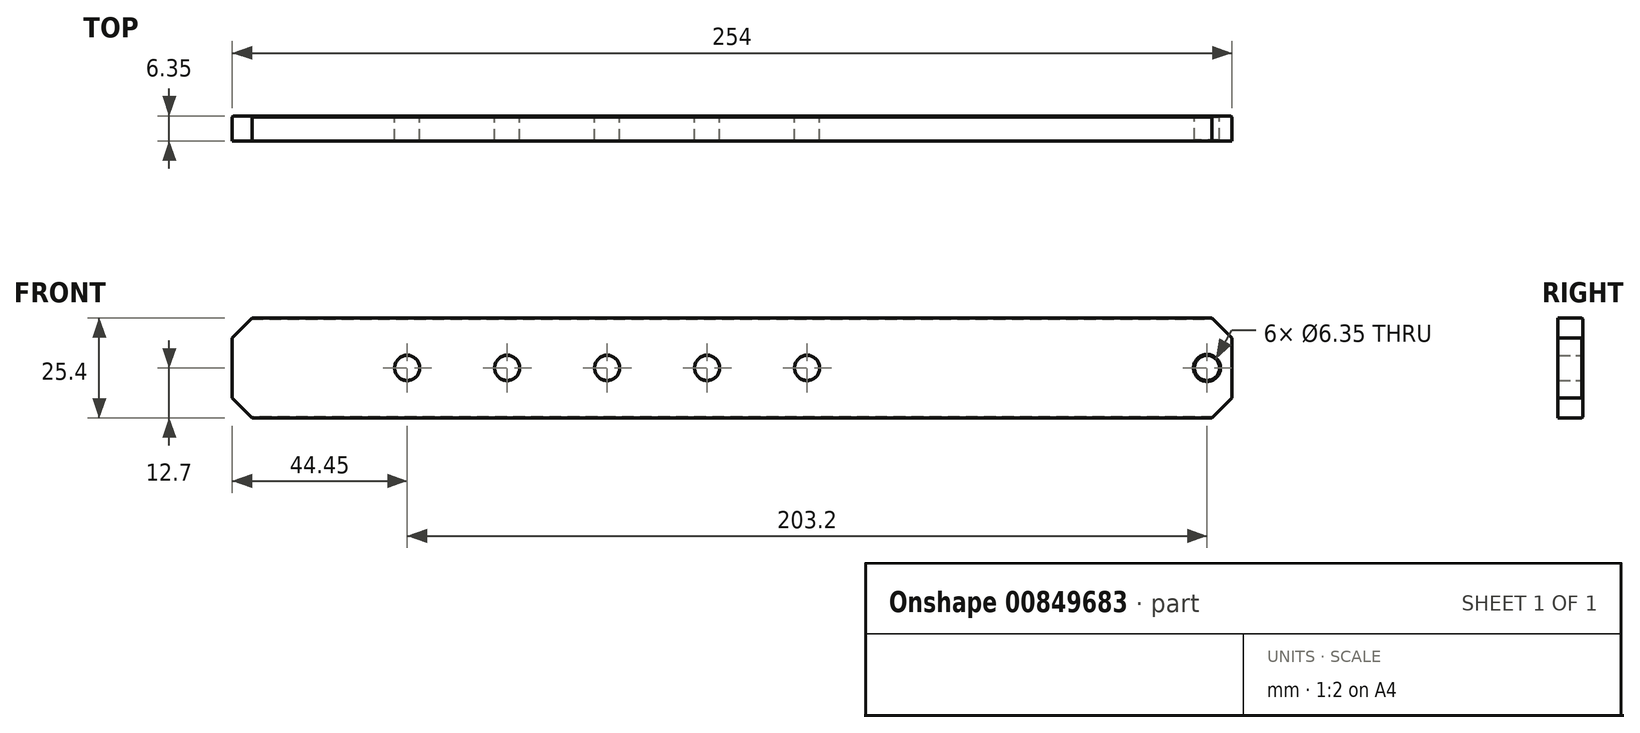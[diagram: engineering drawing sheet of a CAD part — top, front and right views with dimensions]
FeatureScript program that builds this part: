
annotation { "Feature Type Name" : "Feature", "Feature Type Description" : "" }
export const myFeature = defineFeature(function(context is Context, id is Id, definition is map)
    precondition{}
    {
        {
            var Q0;
            Q0=qCreatedBy(makeId("Front.planeOp"),FACE);
            var sketch = newSketch(context, id + "F0", { "sketchPlane" : qUnion([Q0])});
            skLineSegment(sketch, "E0.bottom", {"start": v(127, -12.7) * mm, "end": v(-127, -12.7) * mm});
            skLineSegment(sketch, "E0.top", {"start": v(127, 12.7) * mm, "end": v(-127, 12.7) * mm});
            skLineSegment(sketch, "E0.left", {"start": v(127, -12.7) * mm, "end": v(127, 12.7) * mm});
            skLineSegment(sketch, "E0.right", {"start": v(-127, -12.7) * mm, "end": v(-127, 12.7) * mm});
            skPoint(sketch, "E0.middle", {"position": v(0, 0) * mm});
            skCircle(sketch, "E1", {"center": v(120.65, 0) * mm, "radius": 3.18 * mm});
            skLineSegment(sketch, "E2", {"start": v(120.65, 0) * mm, "end": v(-127, 0) * mm, "construction": true});
            skCircle(sketch, "E3", {"center": v(19.05, 0) * mm, "radius": 3.18 * mm});
            skCircle(sketch, "E4.1.0.0", {"center": v(-6.35, 0) * mm, "radius": 3.18 * mm});
            skCircle(sketch, "E4.2.0.0", {"center": v(-31.75, 0) * mm, "radius": 3.18 * mm});
            skCircle(sketch, "E4.3.0.0", {"center": v(-57.15, 0) * mm, "radius": 3.18 * mm});
            skCircle(sketch, "E4.4.0.0", {"center": v(-82.55, 0) * mm, "radius": 3.18 * mm});
            skLineSegment(sketch, "E4.direction1", {"start": v(19.05, 0) * mm, "end": v(-6.35, 0) * mm, "construction": true});
            skSolve(sketch);
        }
        {
            var Q0;
            Q0 = qSketchRegion(id + "F0", true);
            extrude(context, id + "F1", {"entities" : qUnion([Q0]), "depth" : 6.35 * mm, "offsetDistance" : 25.4 * mm});
        }
        {
            var Q0;
            Q0=makeQuery(id+"F1.opExtrude","CAP_EDGE",EDGE,{"disambiguationData":[OSD([sQuery(id+"F0.wireOp",EDGE,"a60a66de-6e48-4f97-a744-45ec2d759609.0.4.0")])],"isStart":false});
            var Q1;
            Q1=makeQuery(id+"F1.opExtrude","CAP_EDGE",EDGE,{"disambiguationData":[OSD([sQuery(id+"F0.wireOp",EDGE,"d8a7950c-4cc1-41c2-8a6e-5c12bcb3506b.3.0.0")])],"isStart":false});
            var Q2;
            Q2=makeQuery(id+"F1.opExtrude","CAP_EDGE",EDGE,{"disambiguationData":[OSD([sQuery(id+"F0.wireOp",EDGE,"d8a7950c-4cc1-41c2-8a6e-5c12bcb3506b.2.0.0")])],"isStart":false});
            var Q3;
            Q3=makeQuery(id+"F1.opExtrude","CAP_EDGE",EDGE,{"disambiguationData":[OSD([sQuery(id+"F0.wireOp",EDGE,"d8a7950c-4cc1-41c2-8a6e-5c12bcb3506b.1.0.0")])],"isStart":false});
            var Q4;
            Q4=makeQuery(id+"F1.opExtrude","CAP_EDGE",EDGE,{"disambiguationData":[OSD([sQuery(id+"F0.wireOp",EDGE,"ClvN4MZP-DohT-0DrA-vtji-N6Pn7AbvIDh7")])],"isStart":false});
            var Q5;
            Q5=makeQuery(id+"F1.opExtrude","CAP_EDGE",EDGE,{"disambiguationData":[OSD([sQuery(id+"F0.wireOp",EDGE,"E1")])],"isStart":false});
            var Q6;
            Q6=makeQuery(id+"F1.opExtrude","CAP_EDGE",EDGE,{"disambiguationData":[OSD([sQuery(id+"F0.wireOp",EDGE,"E1")])],"isStart":true});
            var Q7;
            Q7=makeQuery(id+"F1.opExtrude","CAP_EDGE",EDGE,{"disambiguationData":[OSD([sQuery(id+"F0.wireOp",EDGE,"ClvN4MZP-DohT-0DrA-vtji-N6Pn7AbvIDh7")])],"isStart":true});
            var Q8;
            Q8=makeQuery(id+"F1.opExtrude","CAP_EDGE",EDGE,{"disambiguationData":[OSD([sQuery(id+"F0.wireOp",EDGE,"d8a7950c-4cc1-41c2-8a6e-5c12bcb3506b.1.0.0")])],"isStart":true});
            var Q9;
            Q9=makeQuery(id+"F1.opExtrude","CAP_FACE",FACE,{"disambiguationData":[OSD([sQuery(id+"F0.wireOp",EDGE,"E0.bottom"),sQuery(id+"F0.wireOp",EDGE,"E0.top"),sQuery(id+"F0.wireOp",EDGE,"E0.left"),sQuery(id+"F0.wireOp",EDGE,"E0.right"),sQuery(id+"F0.wireOp",EDGE,"E1"),sQuery(id+"F0.wireOp",EDGE,"ClvN4MZP-DohT-0DrA-vtji-N6Pn7AbvIDh7"),sQuery(id+"F0.wireOp",EDGE,"d8a7950c-4cc1-41c2-8a6e-5c12bcb3506b.1.0.0"),sQuery(id+"F0.wireOp",EDGE,"d8a7950c-4cc1-41c2-8a6e-5c12bcb3506b.2.0.0"),sQuery(id+"F0.wireOp",EDGE,"d8a7950c-4cc1-41c2-8a6e-5c12bcb3506b.3.0.0"),sQuery(id+"F0.wireOp",EDGE,"a60a66de-6e48-4f97-a744-45ec2d759609.0.4.0")])],"isStart":true});
            chamfer(context, id + "F2", {"entities" : qUnion([Q0, Q1, Q2, Q3, Q4, Q5, Q6, Q7, Q8, Q9]), "width" : 0.25 * mm, "tangentPropagation" : true});
        }
        {
            var Q0;
            Q0=makeQuery(id+"F1.opExtrude","SWEPT_EDGE",EDGE,{"disambiguationData":[OSD([sQuery(id+"F0.wireOp",EDGE,"E0.top"),sQuery(id+"F0.wireOp",EDGE,"E0.right")])]});
            var Q1;
            Q1=makeQuery(id+"F1.opExtrude","SWEPT_EDGE",EDGE,{"disambiguationData":[OSD([sQuery(id+"F0.wireOp",EDGE,"E0.top"),sQuery(id+"F0.wireOp",EDGE,"E0.left")])]});
            var Q2;
            Q2=makeQuery(id+"F1.opExtrude","SWEPT_EDGE",EDGE,{"disambiguationData":[OSD([sQuery(id+"F0.wireOp",EDGE,"E0.bottom"),sQuery(id+"F0.wireOp",EDGE,"E0.left")])]});
            var Q3;
            Q3=makeQuery(id+"F1.opExtrude","SWEPT_EDGE",EDGE,{"disambiguationData":[OSD([sQuery(id+"F0.wireOp",EDGE,"E0.bottom"),sQuery(id+"F0.wireOp",EDGE,"E0.right")])]});
            chamfer(context, id + "F3", {"entities" : qUnion([Q0, Q1, Q2, Q3]), "width" : 5.08 * mm, "tangentPropagation" : true});
        }
        {
            var Q0;
            Q0=qCreatedBy(makeId("Front.planeOp"),FACE);
            cPlane(context, id + "F4", {"entities" : qUnion([Q0]), "cplaneType" : CPlaneType.OFFSET, "offset" : 63.5 * mm, "width" : 152.4 * mm, "height" : 152.4 * mm});
        }
    });
